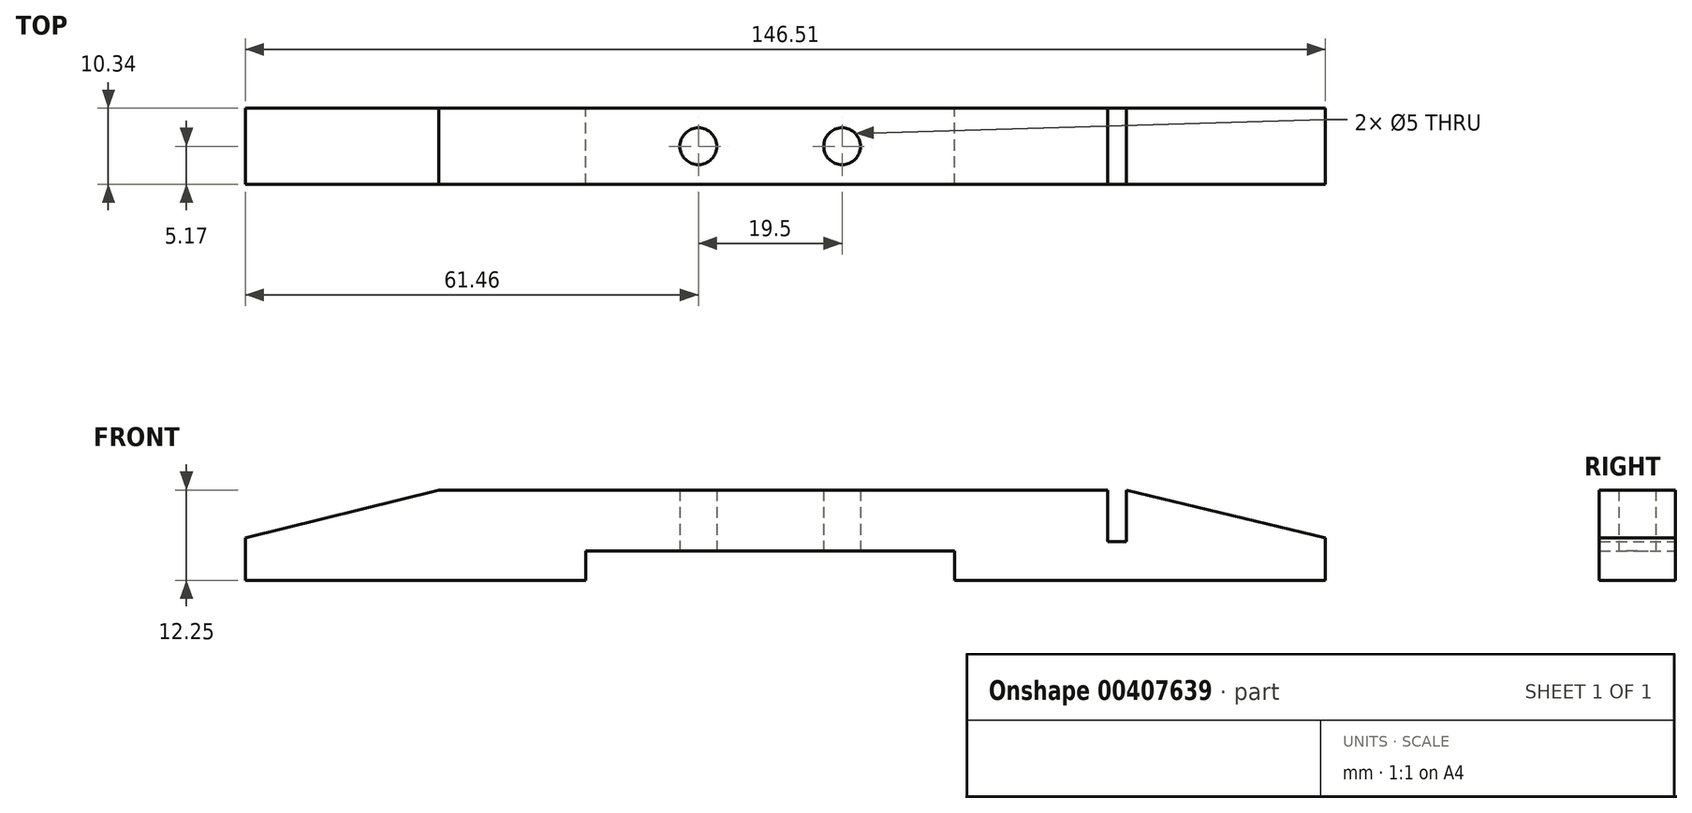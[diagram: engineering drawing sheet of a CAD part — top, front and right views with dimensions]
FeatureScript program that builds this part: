
annotation { "Feature Type Name" : "Feature", "Feature Type Description" : "" }
export const myFeature = defineFeature(function(context is Context, id is Id, definition is map)
    precondition{}
    {
        {
            var Q0;
            Q0=qCreatedBy(makeId("Front.planeOp"),FACE);
            var sketch = newSketch(context, id + "F0", { "sketchPlane" : qUnion([Q0])});
            skLineSegment(sketch, "E0", {"start": v(-25, 4) * mm, "end": v(25, 4) * mm});
            skLineSegment(sketch, "E1", {"start": v(25, 4) * mm, "end": v(25, 0) * mm});
            skLineSegment(sketch, "E2", {"start": v(25, 0) * mm, "end": v(45.8, 0) * mm});
            skLineSegment(sketch, "E3", {"start": v(45.8, 0) * mm, "end": v(45.8, 12.25) * mm});
            skLineSegment(sketch, "E4", {"start": v(45.8, 12.25) * mm, "end": v(-45, 12.25) * mm});
            skLineSegment(sketch, "E5", {"start": v(-45, 12.25) * mm, "end": v(-45, 0) * mm});
            skLineSegment(sketch, "E6", {"start": v(-45, 0) * mm, "end": v(-25, 0) * mm});
            skLineSegment(sketch, "E7", {"start": v(-25, 0) * mm, "end": v(-25, 4) * mm});
            skLineSegment(sketch, "E8", {"start": v(-45, 12.25) * mm, "end": v(-71.2, 5.75) * mm});
            skLineSegment(sketch, "E9", {"start": v(-71.2, 5.75) * mm, "end": v(-71.2, 0) * mm});
            skLineSegment(sketch, "E10", {"start": v(-71.2, 0) * mm, "end": v(-45, 0) * mm});
            skLineSegment(sketch, "E11", {"start": v(45.8, 0) * mm, "end": v(75.3, 0) * mm});
            skLineSegment(sketch, "E12", {"start": v(75.3, 0) * mm, "end": v(75.3, 5.75) * mm});
            skLineSegment(sketch, "E13", {"start": v(75.3, 5.75) * mm, "end": v(48.3, 12.25) * mm});
            skLineSegment(sketch, "E14", {"start": v(48.3, 12.25) * mm, "end": v(48.3, 5.25) * mm});
            skLineSegment(sketch, "E15", {"start": v(48.3, 5.25) * mm, "end": v(45.8, 5.25) * mm});
            skSolve(sketch);
        }
        {
            var Q0;
            Q0=makeQuery(id+"F0.imprint","IMPRINT",FACE,{"disambiguationData":[TD([[makeQuery(id+"F0.imprint","IMPRINT",EDGE,{"derivedFrom":sQuery(id+"F0.wireOp",EDGE,"E0")}),1.0]])]});
            var Q1;
            Q1=makeQuery(id+"F0.imprint","IMPRINT",FACE,{"disambiguationData":[TD([[makeQuery(id+"F0.imprint","IMPRINT",EDGE,{"derivedFrom":sQuery(id+"F0.wireOp",EDGE,"E5")}),-1.0]])]});
            var Q2;
            Q2=makeQuery(id+"F0.imprint","IMPRINT",FACE,{"disambiguationData":[TD([[makeQuery(id+"F0.imprint","IMPRINT",EDGE,{"derivedFrom":sQuery(id+"F0.wireOp",EDGE,"E3")}),-1.0]])]});
            extrude(context, id + "F1", {"entities" : qUnion([Q0, Q1, Q2]), "endBound" : BoundingType.SYMMETRIC, "depth" : 10.35 * mm});
        }
        {
            var Q0;
            Q0=qCreatedBy(makeId("Top.planeOp"),FACE);
            var sketch = newSketch(context, id + "F2", { "sketchPlane" : qUnion([Q0])});
            skCircle(sketch, "E16", {"center": v(9.75, 0) * mm, "radius": 2.5 * mm});
            skCircle(sketch, "E17", {"center": v(-9.75, 0) * mm, "radius": 2.5 * mm});
            skSolve(sketch);
        }
        {
            var Q0;
            Q0 = qSketchRegion(id + "F2", true);
            extrude(context, id + "F3", {"entities" : qUnion([Q0]), "operationType" : NewBodyOperationType.REMOVE, "endBound" : BoundingType.SYMMETRIC, "depth" : 50 * mm});
        }
    });
